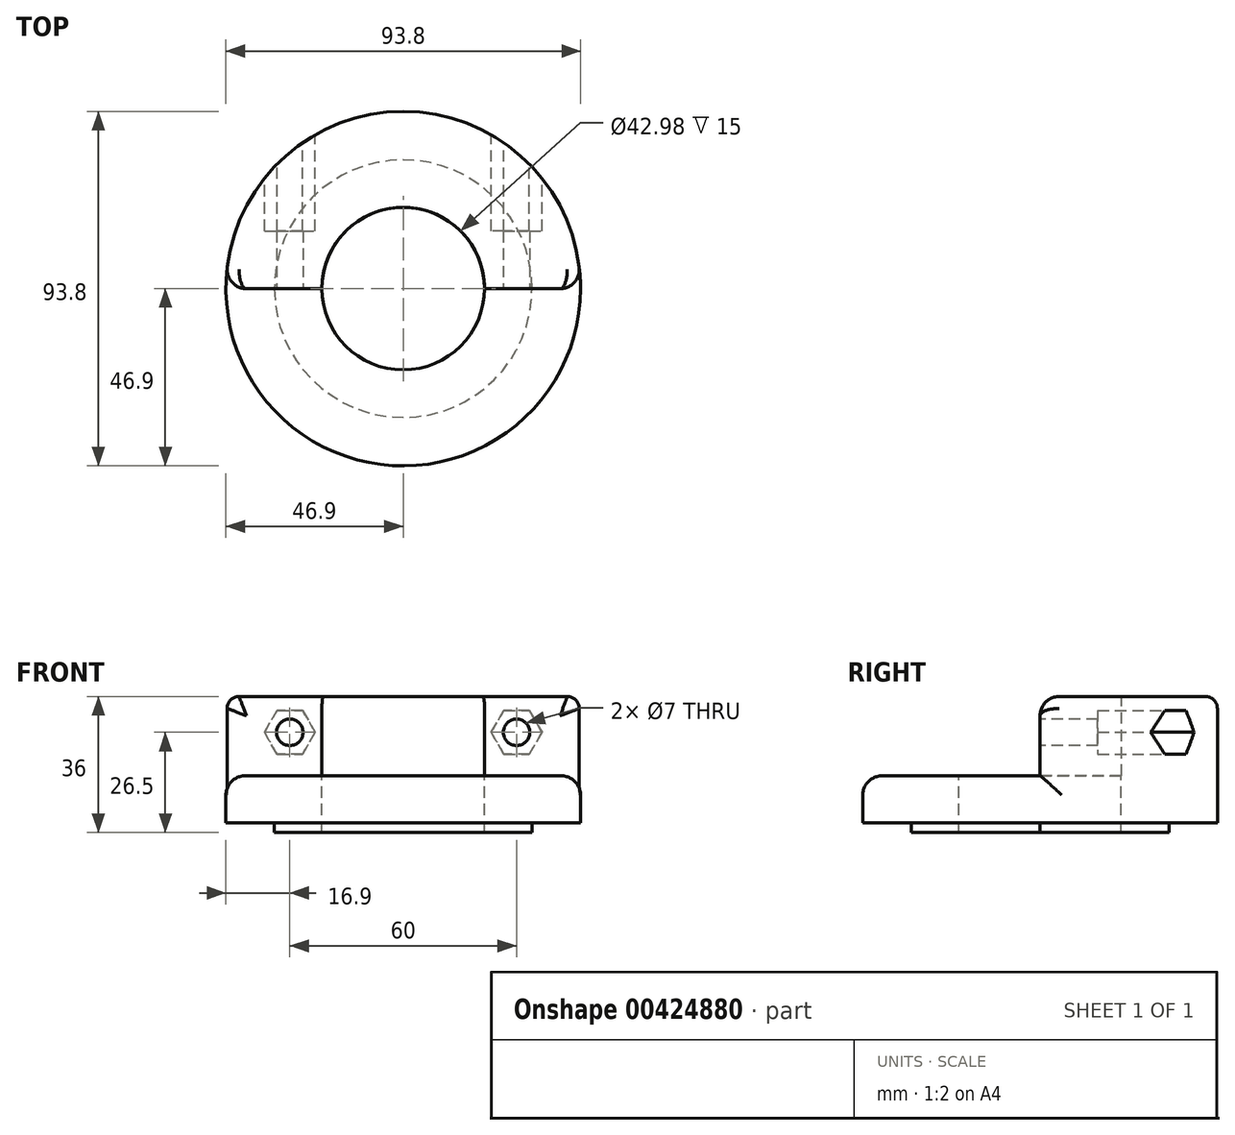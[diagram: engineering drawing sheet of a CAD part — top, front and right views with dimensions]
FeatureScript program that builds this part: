
annotation { "Feature Type Name" : "Feature", "Feature Type Description" : "" }
export const myFeature = defineFeature(function(context is Context, id is Id, definition is map)
    precondition{}
    {
        {
            var Q0;
            Q0=qCreatedBy(makeId("Front.planeOp"),FACE);
            var sketch = newSketch(context, id + "F0", { "sketchPlane" : qUnion([Q0])});
            skLineSegment(sketch, "E0", {"start": v(0, 89.36) * mm, "end": v(0, -89.36) * mm, "construction": true});
            skLineSegment(sketch, "E1.top", {"start": v(21.5, 0) * mm, "end": v(34.07, 0) * mm});
            skPoint(sketch, "E2.visualSharp", {"position": v(46.9, 2.54) * mm});
            skLineSegment(sketch, "E3", {"start": v(34.07, 2.54) * mm, "end": v(46.9, 2.54) * mm});
            skLineSegment(sketch, "E4", {"start": v(46.9, 32.83) * mm, "end": v(46.9, 2.54) * mm});
            skLineSegment(sketch, "E5", {"start": v(21.5, 36) * mm, "end": v(43.73, 36) * mm});
            skLineSegment(sketch, "E6", {"start": v(34.07, 0) * mm, "end": v(34.07, 2.54) * mm});
            skLineSegment(sketch, "E7", {"start": v(-84.1, 0) * mm, "end": v(89.61, 0) * mm, "construction": true});
            skLineSegment(sketch, "E8", {"start": v(21.5, 0) * mm, "end": v(21.5, 36) * mm});
            skPoint(sketch, "E9.visualSharp", {"position": v(46.9, 36) * mm});
            skArc(sketch, "E9.filletArc", {"start": v(46.9, 32.83) * mm, "mid": v(45.97, 35.07) * mm, "end": v(43.73, 36) * mm});
            skSolve(sketch);
        }
        {
            var Q0;
            Q0=makeQuery(id+"F0.imprint","IMPRINT",FACE,{"disambiguationData":[TD([[makeQuery(id+"F0.imprint","IMPRINT",EDGE,{"derivedFrom":sQuery(id+"F0.wireOp",EDGE,"E1.top")}),1.0]])]});
            var Q1;
            Q1=qSketchRegion(id+"F2",true);
            var Q2;
            Q2=sQuery(id+"F0.wireOp",EDGE,"E0");
            revolve(context, id + "F1", {"entities" : qUnion([Q0, Q1]), "axis" : qUnion([Q2]), "revolveType" : RevolveType.TWO_DIRECTIONS, "angle" : 0 * degree, "angleBack" : 180 * degree});
        }
        {
            var Q0;
            Q0=qCreatedBy(makeId("Front.planeOp"),FACE);
            var sketch = newSketch(context, id + "F2", { "sketchPlane" : qUnion([Q0])});
            skLineSegment(sketch, "E10", {"start": v(0, 81.52) * mm, "end": v(0, -79.68) * mm, "construction": true});
            skCircle(sketch, "E11", {"center": v(30, 26.5) * mm, "radius": 3.5 * mm});
            skCircle(sketch, "E12.MirrorC", {"center": v(-30, 26.5) * mm, "radius": 3.5 * mm});
            skSolve(sketch);
        }
        {
            var Q0;
            Q0=qSketchRegion(id+"F2",true);
            extrude(context, id + "F3", {"entities" : qUnion([Q0]), "operationType" : NewBodyOperationType.REMOVE, "oppositeDirection" : true, "depth" : 53.34 * mm, "hasSecondDirection" : true, "secondDirectionOppositeDirection" : false, "secondDirectionDepth" : 2.54 * mm});
        }
        {
            var Q0;
            Q0=qCreatedBy(makeId("Front.planeOp"),FACE);
            cPlane(context, id + "F4", {"entities" : qUnion([Q0]), "cplaneType" : CPlaneType.OFFSET, "offset" : 50.8 * mm, "oppositeDirection" : true, "width" : 152.4 * mm, "height" : 152.4 * mm});
        }
        {
            var Q0;
            Q0=qCreatedBy(id+"F4.planeOp",FACE);
            var sketch = newSketch(context, id + "F5", { "sketchPlane" : qUnion([Q0])});
            skLineSegment(sketch, "E13", {"start": v(0, 83.45) * mm, "end": v(0, -83.48) * mm, "construction": true});
            skPoint(sketch, "E14", {"position": v(30, 26.5) * mm});
            skCircle(sketch, "E15.cCircle", {"center": v(30, 26.5) * mm, "radius": 5.8 * mm, "construction": true});
            skLineSegment(sketch, "E15.0", {"start": v(33.35, 32.3) * mm, "end": v(36.7, 26.5) * mm});
            skLineSegment(sketch, "E15.1", {"start": v(36.7, 26.5) * mm, "end": v(33.35, 20.7) * mm});
            skLineSegment(sketch, "E15.2", {"start": v(33.35, 20.7) * mm, "end": v(26.65, 20.7) * mm});
            skLineSegment(sketch, "E15.3", {"start": v(26.65, 20.7) * mm, "end": v(23.3, 26.5) * mm});
            skLineSegment(sketch, "E15.4", {"start": v(23.3, 26.5) * mm, "end": v(26.65, 32.3) * mm});
            skLineSegment(sketch, "E15.5", {"start": v(26.65, 32.3) * mm, "end": v(33.35, 32.3) * mm});
            skPoint(sketch, "E15.0.midPoint", {"position": v(35.02, 29.4) * mm});
            skPoint(sketch, "E16", {"position": v(-30, 26.5) * mm});
            skCircle(sketch, "E17.cCircle", {"center": v(-30, 26.5) * mm, "radius": 5.8 * mm, "construction": true});
            skLineSegment(sketch, "E17.0", {"start": v(-36.7, 26.5) * mm, "end": v(-33.35, 32.3) * mm});
            skLineSegment(sketch, "E17.1", {"start": v(-33.35, 32.3) * mm, "end": v(-26.65, 32.3) * mm});
            skLineSegment(sketch, "E17.2", {"start": v(-26.65, 32.3) * mm, "end": v(-23.3, 26.5) * mm});
            skLineSegment(sketch, "E17.3", {"start": v(-23.3, 26.5) * mm, "end": v(-26.65, 20.7) * mm});
            skLineSegment(sketch, "E17.4", {"start": v(-26.65, 20.7) * mm, "end": v(-33.35, 20.7) * mm});
            skLineSegment(sketch, "E17.5", {"start": v(-33.35, 20.7) * mm, "end": v(-36.7, 26.5) * mm});
            skPoint(sketch, "E17.0.midPoint", {"position": v(-35.02, 29.4) * mm});
            skSolve(sketch);
        }
        {
            var Q0;
            Q0=makeQuery(id+"F5.imprint","IMPRINT",FACE,{"disambiguationData":[TD([[makeQuery(id+"F5.imprint","IMPRINT",EDGE,{"derivedFrom":sQuery(id+"F5.wireOp",EDGE,"E15.0")}),-1.0]])]});
            var Q1;
            Q1=makeQuery(id+"F5.imprint","IMPRINT",FACE,{"disambiguationData":[TD([[makeQuery(id+"F5.imprint","IMPRINT",EDGE,{"derivedFrom":sQuery(id+"F5.wireOp",EDGE,"E17.0")}),-1.0]])]});
            var Q2;
            Q2=qSketchRegion(id+"FJtj0piFx7HUNcg_1",true);
            extrude(context, id + "F6", {"entities" : qUnion([Q0, Q1, Q2]), "operationType" : NewBodyOperationType.REMOVE, "depth" : 35.56 * mm});
        }
        {
            var Q0;
            Q0=qCreatedBy(makeId("Front.planeOp"),FACE);
            var sketch = newSketch(context, id + "F7", { "sketchPlane" : qUnion([Q0])});
            skLineSegment(sketch, "E18", {"start": v(-21.49, 15) * mm, "end": v(-21.49, 0) * mm});
            skLineSegment(sketch, "E19", {"start": v(-21.49, 0) * mm, "end": v(-34.06, 0) * mm});
            skLineSegment(sketch, "E20", {"start": v(-34.06, 0) * mm, "end": v(-34.06, 2.54) * mm});
            skLineSegment(sketch, "E21", {"start": v(-34.06, 2.54) * mm, "end": v(-46.9, 2.54) * mm});
            skLineSegment(sketch, "E22", {"start": v(-46.9, 2.54) * mm, "end": v(-46.9, 15) * mm});
            skLineSegment(sketch, "E23", {"start": v(-46.9, 15) * mm, "end": v(-21.49, 15) * mm});
            skLineSegment(sketch, "E24", {"start": v(0, 79.82) * mm, "end": v(0, -79.52) * mm, "construction": true});
            skSolve(sketch);
        }
        {
            var Q0;
            Q0=makeQuery(id+"F7.imprint","IMPRINT",FACE,{"disambiguationData":[TD([[makeQuery(id+"F7.imprint","IMPRINT",EDGE,{"derivedFrom":sQuery(id+"F7.wireOp",EDGE,"E18")}),-1.0]])]});
            var Q1;
            Q1=sQuery(id+"F7.wireOp",EDGE,"E24");
            revolve(context, id + "F8", {"operationType" : NewBodyOperationType.ADD, "entities" : qUnion([Q0]), "axis" : qUnion([Q1]), "revolveType" : RevolveType.FULL});
        }
        {
            var Q0;
            Q0=makeQuery(id+"F8.opRevolve","SWEPT_EDGE",EDGE,{"disambiguationData":[OSD([sQuery(id+"F7.wireOp",EDGE,"E22"),sQuery(id+"F7.wireOp",EDGE,"E23")])]});
            var Q1;
            Q1=makeQuery(id+"F1.opRevolve","CAP_EDGE",EDGE,{"disambiguationData":[OSD([sQuery(id+"F0.wireOp",EDGE,"E4")])],"isStart":true});
            var Q2;
            Q2=makeQuery(id+"F1.opRevolve","CAP_EDGE",EDGE,{"disambiguationData":[OSD([sQuery(id+"F0.wireOp",EDGE,"E4")])],"isStart":false});
            var Q3;
            Q3=makeQuery(id+"F1.opRevolve","CAP_EDGE",EDGE,{"disambiguationData":[OSD([sQuery(id+"F0.wireOp",EDGE,"E5")])],"isStart":false});
            fillet(context, id + "F9", {"entities" : qUnion([Q0, Q1, Q2, Q3]), "radius" : 5.08 * mm, "tangentPropagation" : true, "allowEdgeOverflow" : false});
        }
    });
